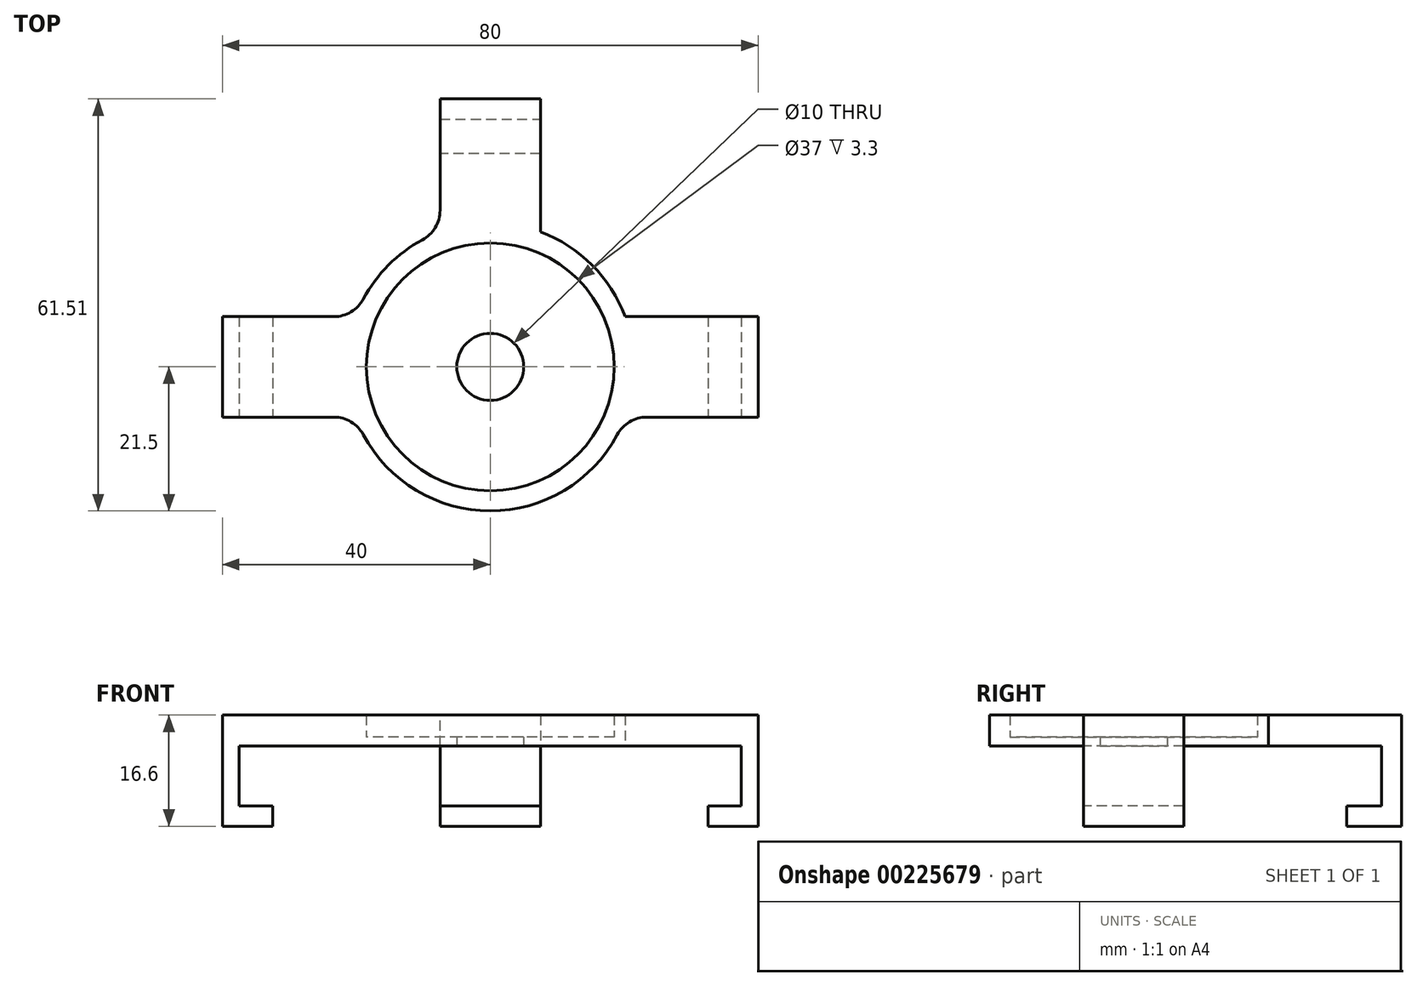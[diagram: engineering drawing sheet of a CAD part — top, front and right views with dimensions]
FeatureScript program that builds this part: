
annotation { "Feature Type Name" : "Feature", "Feature Type Description" : "" }
export const myFeature = defineFeature(function(context is Context, id is Id, definition is map)
    precondition{}
    {
        {
            var Q0;
            Q0=qCreatedBy(makeId("Top.planeOp"),FACE);
            var sketch = newSketch(context, id + "F0", { "sketchPlane" : qUnion([Q0])});
            skCircle(sketch, "E0", {"center": v(0, 0) * mm, "radius": 21.5 * mm});
            skCircle(sketch, "E1", {"center": v(0, 0) * mm, "radius": 18.5 * mm});
            skPoint(sketch, "E2.top.end.orphan", {"position": v(-7.5, -36.83) * mm});
            skPoint(sketch, "E3.orphan", {"position": v(7.5, -37) * mm});
            skLineSegment(sketch, "E4.top", {"start": v(-7.5, 40) * mm, "end": v(7.5, 40) * mm});
            skCircle(sketch, "E5", {"center": v(0, 0) * mm, "radius": 5 * mm});
            skLineSegment(sketch, "E6.top", {"start": v(7.5, 31.83) * mm, "end": v(-7.5, 31.83) * mm});
            skLineSegment(sketch, "E7.bottom", {"start": v(-37.5, 7.5) * mm, "end": v(-20.15, 7.5) * mm});
            skLineSegment(sketch, "E7.top", {"start": v(-37.5, -7.5) * mm, "end": v(-20.15, -7.5) * mm});
            skLineSegment(sketch, "E7.left", {"start": v(-37.5, 7.5) * mm, "end": v(-37.5, -7.5) * mm});
            skLineSegment(sketch, "E7.right", {"start": v(37.5, 7.5) * mm, "end": v(37.5, -7.5) * mm});
            skLineSegment(sketch, "E8.bottom", {"start": v(-37.5, 7.5) * mm, "end": v(-40, 7.5) * mm});
            skLineSegment(sketch, "E8.top", {"start": v(-37.5, -7.5) * mm, "end": v(-40, -7.5) * mm});
            skLineSegment(sketch, "E8.right", {"start": v(-40, 7.5) * mm, "end": v(-40, -7.5) * mm});
            skLineSegment(sketch, "E9.bottom", {"start": v(37.5, 7.5) * mm, "end": v(40, 7.5) * mm});
            skLineSegment(sketch, "E9.top", {"start": v(37.5, -7.5) * mm, "end": v(40, -7.5) * mm});
            skLineSegment(sketch, "E9.right", {"start": v(40, 7.5) * mm, "end": v(40, -7.5) * mm});
            skLineSegment(sketch, "E10.bottom", {"start": v(-37.5, 7.5) * mm, "end": v(-32.5, 7.5) * mm});
            skLineSegment(sketch, "E10.top", {"start": v(-37.5, -7.5) * mm, "end": v(-32.5, -7.5) * mm});
            skLineSegment(sketch, "E10.right", {"start": v(-32.5, 7.5) * mm, "end": v(-32.5, -7.5) * mm});
            skLineSegment(sketch, "E11.bottom", {"start": v(37.5, 7.5) * mm, "end": v(32.5, 7.5) * mm});
            skLineSegment(sketch, "E11.top", {"start": v(37.5, -7.5) * mm, "end": v(32.5, -7.5) * mm});
            skLineSegment(sketch, "E11.right", {"start": v(32.5, 7.5) * mm, "end": v(32.5, -7.5) * mm});
            skLineSegment(sketch, "E12.trimOffspring", {"start": v(20.15, 7.5) * mm, "end": v(37.5, 7.5) * mm});
            skLineSegment(sketch, "E13.trimOffspring", {"start": v(20.15, -7.5) * mm, "end": v(37.5, -7.5) * mm});
            skLineSegment(sketch, "E14.top", {"start": v(-7.5, 37) * mm, "end": v(7.5, 37) * mm});
            skLineSegment(sketch, "E15", {"start": v(-7.5, 40) * mm, "end": v(-7.5, 37) * mm});
            skLineSegment(sketch, "E16", {"start": v(-7.5, 37) * mm, "end": v(-7.5, 31.83) * mm});
            skLineSegment(sketch, "E17", {"start": v(-7.5, 31.83) * mm, "end": v(-7.5, 20.15) * mm});
            skLineSegment(sketch, "E18", {"start": v(7.5, 40) * mm, "end": v(7.5, 37) * mm});
            skLineSegment(sketch, "E19", {"start": v(7.5, 37) * mm, "end": v(7.5, 31.83) * mm});
            skLineSegment(sketch, "E20", {"start": v(7.5, 20.15) * mm, "end": v(7.5, 31.83) * mm});
            skSolve(sketch);
        }
        {
            var Q0;
            Q0=makeQuery(id+"F0.imprint","IMPRINT",FACE,{"disambiguationData":[TD([[makeQuery(id+"F0.imprint","IMPRINT",EDGE,{"derivedFrom":sQuery(id+"F0.wireOp",EDGE,"E1")}),-1.0]])]});
            var Q1;
            Q1=makeQuery(id+"F0.imprint","IMPRINT",FACE,{"disambiguationData":[TD([[makeQuery(id+"F0.imprint","IMPRINT",EDGE,{"derivedFrom":sQuery(id+"F0.wireOp",EDGE,"E1")}),1.0]])]});
            extrude(context, id + "F1", {"entities" : qUnion([Q0, Q1]), "depth" : 1.3 * mm});
        }
        {
            var Q0;
            Q0=makeQuery(id+"F0.imprint","IMPRINT",FACE,{"disambiguationData":[TD([[makeQuery(id+"F0.imprint","IMPRINT",EDGE,{"derivedFrom":sQuery(id+"F0.wireOp",EDGE,"E1")}),-1.0]])]});
            extrude(context, id + "F2", {"entities" : qUnion([Q0]), "operationType" : NewBodyOperationType.ADD, "depth" : 4.6 * mm});
        }
        {
            var Q0;
            Q0=makeQuery(id+"F0.imprint","IMPRINT",FACE,{"disambiguationData":[TD([[makeQuery(id+"F0.imprint","IMPRINT",EDGE,{"derivedFrom":sQuery(id+"F0.wireOp",EDGE,"E4.top")}),-1.0]])]});
            var Q1;
            Q1=makeQuery(id+"F0.imprint","IMPRINT",FACE,{"disambiguationData":[TD([[makeQuery(id+"F0.imprint","IMPRINT",EDGE,{"derivedFrom":sQuery(id+"F0.wireOp",EDGE,"E6.top")}),-1.0]])]});
            var Q2;
            Q2=makeQuery(id+"F0.imprint","IMPRINT",FACE,{"disambiguationData":[TD([[makeQuery(id+"F0.imprint","IMPRINT",EDGE,{"derivedFrom":sQuery(id+"F0.wireOp",EDGE,"E6.top")}),1.0]])]});
            var Q3;
            Q3=makeQuery(id+"F0.imprint","IMPRINT",FACE,{"disambiguationData":[TD([[makeQuery(id+"F0.imprint","IMPRINT",EDGE,{"derivedFrom":sQuery(id+"F0.wireOp",EDGE,"E8.bottom")}),1.0]])]});
            var Q4;
            Q4=makeQuery(id+"F0.imprint","IMPRINT",FACE,{"disambiguationData":[TD([[makeQuery(id+"F0.imprint","IMPRINT",EDGE,{"derivedFrom":sQuery(id+"F0.wireOp",EDGE,"E7.left")}),1.0]])]});
            var Q5;
            {var subQ0=sQuery(id+"F0.wireOp",EDGE,"E7.bottom");Q5=makeQuery(id+"F0.imprint","IMPRINT",FACE,{"disambiguationData":[TD([[makeQuery(id+"F0.imprint","IMPRINT",EDGE,{"derivedFrom":subQ0}),-1.0]])]});}
            var Q6;
            {var subQ5=sQuery(id+"F0.wireOp",EDGE,"E11.right");Q6=makeQuery(id+"F0.imprint","IMPRINT",FACE,{"disambiguationData":[TD([[makeQuery(id+"F0.imprint","IMPRINT",EDGE,{"derivedFrom":subQ5}),-1.0]])]});}
            var Q7;
            {var subQ0=sQuery(id+"F0.wireOp",EDGE,"E7.right");Q7=makeQuery(id+"F0.imprint","IMPRINT",FACE,{"disambiguationData":[TD([[makeQuery(id+"F0.imprint","IMPRINT",EDGE,{"derivedFrom":subQ0}),-1.0]])]});}
            var Q8;
            Q8=makeQuery(id+"F0.imprint","IMPRINT",FACE,{"disambiguationData":[TD([[makeQuery(id+"F0.imprint","IMPRINT",EDGE,{"derivedFrom":sQuery(id+"F0.wireOp",EDGE,"E9.bottom")}),-1.0]])]});
            extrude(context, id + "F3", {"entities" : qUnion([Q0, Q1, Q2, Q3, Q4, Q5, Q6, Q7, Q8]), "operationType" : NewBodyOperationType.ADD, "depth" : 4.6 * mm});
        }
        {
            var Q0;
            Q0=makeQuery(id+"F0.imprint","IMPRINT",FACE,{"disambiguationData":[TD([[makeQuery(id+"F0.imprint","IMPRINT",EDGE,{"derivedFrom":sQuery(id+"F0.wireOp",EDGE,"E6.top")}),-1.0]])]});
            var Q1;
            Q1=makeQuery(id+"F0.imprint","IMPRINT",FACE,{"disambiguationData":[TD([[makeQuery(id+"F0.imprint","IMPRINT",EDGE,{"derivedFrom":sQuery(id+"F0.wireOp",EDGE,"E4.top")}),-1.0]])]});
            var Q2;
            Q2=makeQuery(id+"F0.imprint","IMPRINT",FACE,{"disambiguationData":[TD([[makeQuery(id+"F0.imprint","IMPRINT",EDGE,{"derivedFrom":sQuery(id+"F0.wireOp",EDGE,"E9.bottom")}),-1.0]])]});
            var Q3;
            {var subQ0=sQuery(id+"F0.wireOp",EDGE,"E7.right");Q3=makeQuery(id+"F0.imprint","IMPRINT",FACE,{"disambiguationData":[TD([[makeQuery(id+"F0.imprint","IMPRINT",EDGE,{"derivedFrom":subQ0}),-1.0]])]});}
            var Q4;
            Q4=makeQuery(id+"F0.imprint","IMPRINT",FACE,{"disambiguationData":[TD([[makeQuery(id+"F0.imprint","IMPRINT",EDGE,{"derivedFrom":sQuery(id+"F0.wireOp",EDGE,"E7.left")}),1.0]])]});
            var Q5;
            Q5=makeQuery(id+"F0.imprint","IMPRINT",FACE,{"disambiguationData":[TD([[makeQuery(id+"F0.imprint","IMPRINT",EDGE,{"derivedFrom":sQuery(id+"F0.wireOp",EDGE,"E8.bottom")}),1.0]])]});
            extrude(context, id + "F4", {"entities" : qUnion([Q0, Q1, Q2, Q3, Q4, Q5]), "operationType" : NewBodyOperationType.ADD, "oppositeDirection" : true, "depth" : 12 * mm});
        }
        {
            var Q0;
            {var subQ0=sQuery(id+"F0.wireOp",EDGE,"E7.right");Q0=makeQuery(id+"F0.imprint","IMPRINT",FACE,{"disambiguationData":[TD([[makeQuery(id+"F0.imprint","IMPRINT",EDGE,{"derivedFrom":subQ0}),-1.0]])]});}
            var Q1;
            Q1=makeQuery(id+"F0.imprint","IMPRINT",FACE,{"disambiguationData":[TD([[makeQuery(id+"F0.imprint","IMPRINT",EDGE,{"derivedFrom":sQuery(id+"F0.wireOp",EDGE,"E7.left")}),1.0]])]});
            var Q2;
            Q2=makeQuery(id+"F0.imprint","IMPRINT",FACE,{"disambiguationData":[TD([[makeQuery(id+"F0.imprint","IMPRINT",EDGE,{"derivedFrom":sQuery(id+"F0.wireOp",EDGE,"E6.top")}),-1.0]])]});
            extrude(context, id + "F5", {"entities" : qUnion([Q0, Q1, Q2]), "operationType" : NewBodyOperationType.REMOVE, "oppositeDirection" : true, "depth" : 9 * mm});
        }
        {
            var Q0;
            Q0=makeQuery(id+"F3.opExtrude","SWEPT_EDGE",EDGE,{"disambiguationData":[OSD([sQuery(id+"F0.wireOp",EDGE,"E0"),sQuery(id+"F0.wireOp",EDGE,"E20")])]});
            var Q1;
            Q1=makeQuery(id+"F3.opExtrude","SWEPT_EDGE",EDGE,{"disambiguationData":[OSD([sQuery(id+"F0.wireOp",EDGE,"E0"),sQuery(id+"F0.wireOp",EDGE,"E13.trimOffspring")])]});
            var Q2;
            Q2=makeQuery(id+"F3.opExtrude","SWEPT_EDGE",EDGE,{"disambiguationData":[OSD([sQuery(id+"F0.wireOp",EDGE,"E0"),sQuery(id+"F0.wireOp",EDGE,"E12.trimOffspring")])]});
            var Q3;
            Q3=makeQuery(id+"F3.opExtrude","SWEPT_EDGE",EDGE,{"disambiguationData":[OSD([sQuery(id+"F0.wireOp",EDGE,"E0"),sQuery(id+"F0.wireOp",EDGE,"E17")])]});
            var Q4;
            Q4=makeQuery(id+"F3.opExtrude","SWEPT_EDGE",EDGE,{"disambiguationData":[OSD([sQuery(id+"F0.wireOp",EDGE,"E0"),sQuery(id+"F0.wireOp",EDGE,"E7.bottom")])]});
            var Q5;
            Q5=makeQuery(id+"F3.opExtrude","SWEPT_EDGE",EDGE,{"disambiguationData":[OSD([sQuery(id+"F0.wireOp",EDGE,"E0"),sQuery(id+"F0.wireOp",EDGE,"E7.top")])]});
            fillet(context, id + "F6", {"entities" : qUnion([Q0, Q1, Q2, Q3, Q4, Q5]), "radius" : 5 * mm, "tangentPropagation" : true, "allowEdgeOverflow" : false});
        }
    });
